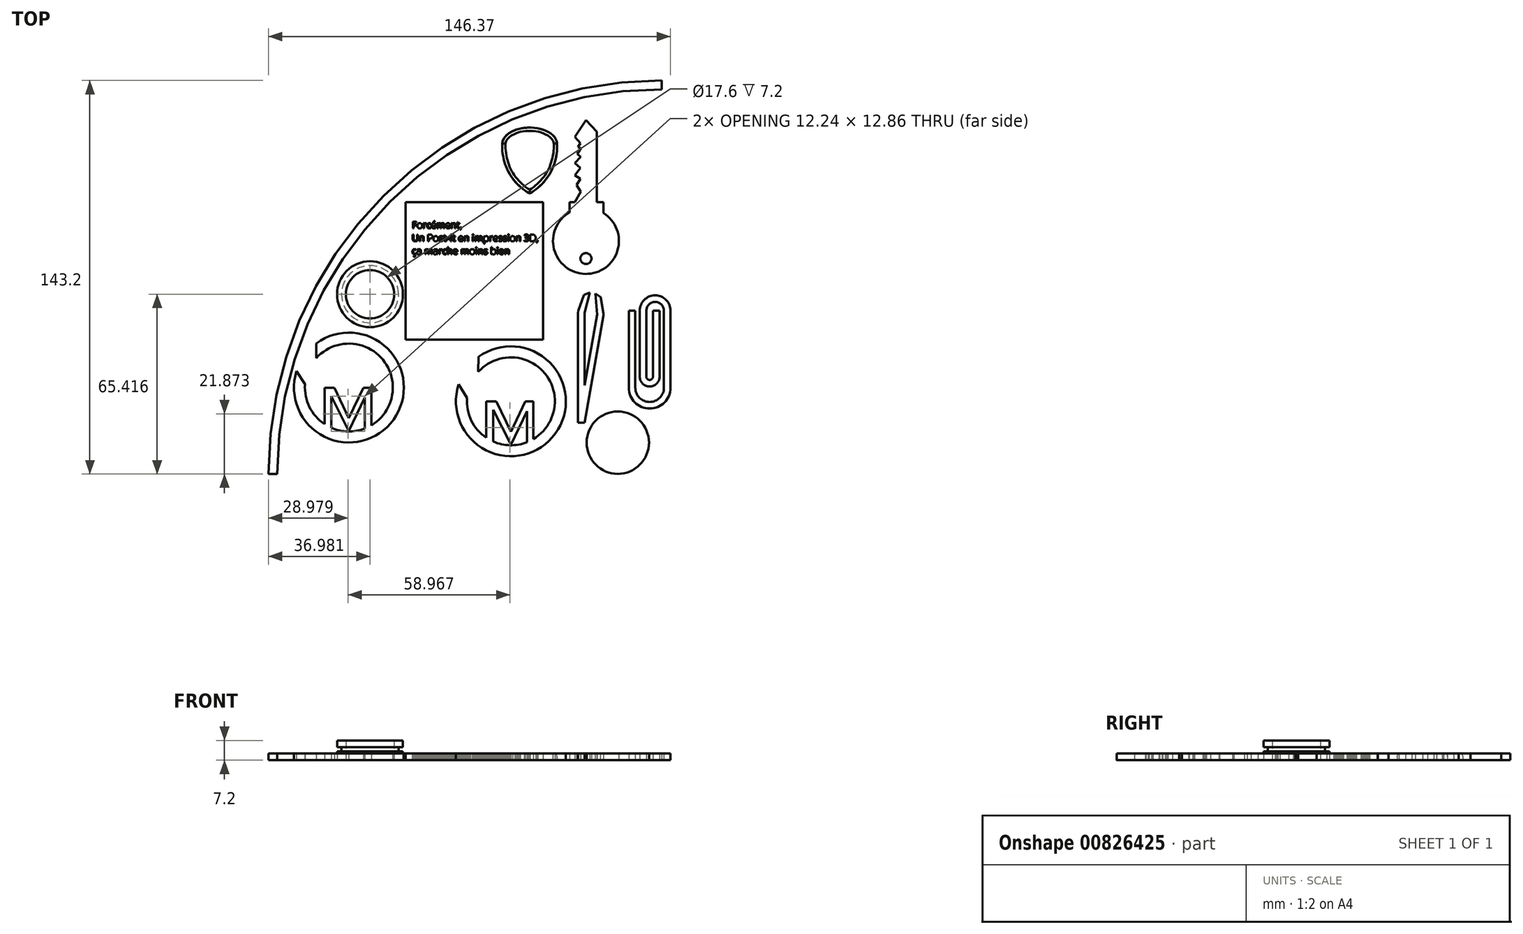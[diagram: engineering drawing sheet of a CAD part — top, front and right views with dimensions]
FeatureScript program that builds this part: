
annotation { "Feature Type Name" : "Feature", "Feature Type Description" : "" }
export const myFeature = defineFeature(function(context is Context, id is Id, definition is map)
    precondition{}
    {
        {
            var Q0;
            Q0=qCreatedBy(makeId("Top.planeOp"),FACE);
            var sketch = newSketch(context, id + "F0", { "sketchPlane" : qUnion([Q0])});
            skArc(sketch, "E0", {"start": v(69.34, 66.2) * mm, "mid": v(-29.65, 25.2) * mm, "end": v(-70.66, -73.8) * mm});
            skArc(sketch, "E1.0", {"start": v(69.34, 69.4) * mm, "mid": v(-31.91, 27.47) * mm, "end": v(-73.86, -73.8) * mm});
            skLineSegment(sketch, "E2", {"start": v(-70.66, -73.8) * mm, "end": v(-73.86, -73.8) * mm});
            skLineSegment(sketch, "E3", {"start": v(69.34, 66.2) * mm, "end": v(69.34, 69.4) * mm});
            skLineSegment(sketch, "E4.bottom", {"start": v(58.9, 56.22) * mm, "end": v(55.7, 56.22) * mm});
            skLineSegment(sketch, "E4.top", {"start": v(58.9, 24.22) * mm, "end": v(55.7, 24.22) * mm});
            skLineSegment(sketch, "E4.right", {"start": v(55.7, 56.22) * mm, "end": v(55.7, 24.22) * mm});
            skPoint(sketch, "E5.end.orphan", {"position": v(61.85, 21.02) * mm});
            skPoint(sketch, "E6.end.orphan", {"position": v(65.05, 21.02) * mm});
            skCircle(sketch, "E7", {"center": v(41.73, 11) * mm, "radius": 12 * mm});
            skCircle(sketch, "E8", {"center": v(41.73, 4.6) * mm, "radius": 2 * mm});
            skLineSegment(sketch, "E9", {"start": v(41.73, 11) * mm, "end": v(41.73, 55) * mm});
            skLineSegment(sketch, "E10", {"start": v(35.73, 25.17) * mm, "end": v(35.73, 21.4) * mm});
            skLineSegment(sketch, "E11", {"start": v(48.13, 25.17) * mm, "end": v(48.13, 21.15) * mm});
            skLineSegment(sketch, "E12", {"start": v(48.13, 25.17) * mm, "end": v(35.73, 25.17) * mm});
            skLineSegment(sketch, "E13", {"start": v(41.73, 25.17) * mm, "end": v(45.73, 25.17) * mm});
            skPoint(sketch, "E13.startSnap0", {"position": v(41.93, 25.17) * mm});
            skLineSegment(sketch, "E14", {"start": v(45.73, 25.17) * mm, "end": v(37.73, 25.17) * mm});
            skLineSegment(sketch, "E15.bottom", {"start": v(37.73, 25.17) * mm, "end": v(45.73, 25.17) * mm});
            skLineSegment(sketch, "E15.top", {"start": v(37.73, 25.17) * mm, "end": v(45.73, 25.17) * mm});
            skLineSegment(sketch, "E15.left", {"start": v(21.23, 18.77) * mm, "end": v(21.23, 18.77) * mm});
            skLineSegment(sketch, "E15.right", {"start": v(29.23, 18.77) * mm, "end": v(29.23, 18.77) * mm});
            skLineSegment(sketch, "E16", {"start": v(45.73, 25.17) * mm, "end": v(45.73, 50.72) * mm});
            skLineSegment(sketch, "E17", {"start": v(37.73, 40.09) * mm, "end": v(37.73, 39.31) * mm});
            skLineSegment(sketch, "E18", {"start": v(41.73, 55) * mm, "end": v(37.73, 48.82) * mm});
            skLineSegment(sketch, "E19", {"start": v(37.73, 48.82) * mm, "end": v(41.73, 55) * mm});
            skLineSegment(sketch, "E20", {"start": v(41.73, 55) * mm, "end": v(45.73, 50.72) * mm});
            skLineSegment(sketch, "E21", {"start": v(37.73, 48.82) * mm, "end": v(39.73, 46.63) * mm});
            skPoint(sketch, "E21.endSnap0", {"position": v(39.73, 51.91) * mm});
            skLineSegment(sketch, "E22", {"start": v(39.73, 46.63) * mm, "end": v(38.83, 45.25) * mm});
            skLineSegment(sketch, "E23", {"start": v(38.83, 45.25) * mm, "end": v(39.77, 44.64) * mm});
            skLineSegment(sketch, "E24", {"start": v(39.77, 44.64) * mm, "end": v(38.53, 42.71) * mm});
            skLineSegment(sketch, "E25", {"start": v(38.53, 42.71) * mm, "end": v(39.77, 41.6) * mm});
            skLineSegment(sketch, "E26", {"start": v(39.77, 41.6) * mm, "end": v(37.73, 39.31) * mm});
            skPoint(sketch, "E26.endSnap0", {"position": v(37.73, 40.09) * mm});
            skLineSegment(sketch, "E27", {"start": v(37.73, 39.31) * mm, "end": v(39.73, 37.53) * mm});
            skLineSegment(sketch, "E28", {"start": v(39.73, 37.53) * mm, "end": v(37.73, 34.88) * mm});
            skLineSegment(sketch, "E29", {"start": v(37.73, 34.88) * mm, "end": v(39.73, 33.59) * mm});
            skLineSegment(sketch, "E30", {"start": v(39.73, 33.59) * mm, "end": v(38.32, 31.4) * mm});
            skLineSegment(sketch, "E31", {"start": v(38.32, 31.4) * mm, "end": v(39.77, 28.88) * mm});
            skLineSegment(sketch, "E32", {"start": v(39.77, 28.88) * mm, "end": v(37.73, 25.17) * mm});
            skLineSegment(sketch, "E33", {"start": v(41.73, 25.17) * mm, "end": v(40.93, 25.17) * mm});
            skLineSegment(sketch, "E34", {"start": v(40.93, 25.17) * mm, "end": v(42.53, 25.17) * mm});
            skLineSegment(sketch, "E35", {"start": v(42.53, 25.17) * mm, "end": v(42.53, 54.15) * mm});
            skLineSegment(sketch, "E36", {"start": v(41.17, 54.15) * mm, "end": v(40.93, 25.17) * mm});
            skPoint(sketch, "E37.orphan", {"position": v(37.73, 55) * mm});
            skCircle(sketch, "E38", {"center": v(53.3, -62.4) * mm, "radius": 11.35 * mm});
            skCircle(sketch, "E39", {"center": v(-36.88, -8.37) * mm, "radius": 8.8 * mm});
            skCircle(sketch, "E40", {"center": v(-36.88, -8.37) * mm, "radius": 12 * mm});
            skEllipticalArc(sketch, "E41", {});
            skEllipticalArc(sketch, "E42", {});
            skPoint(sketch, "E43", {"position": v(11.23, 39.87) * mm});
            skPoint(sketch, "E44", {"position": v(12.95, 43.23) * mm});
            skPoint(sketch, "E45", {"position": v(29.5, 43.23) * mm});
            skPoint(sketch, "E46", {"position": v(31.23, 39.87) * mm});
            skEllipticalArc(sketch, "E47.trimOffspring", {});
            skLineSegment(sketch, "E48.bottom", {"start": v(26.09, 25.12) * mm, "end": v(-23.91, 25.12) * mm});
            skLineSegment(sketch, "E48.top", {"start": v(26.09, -24.88) * mm, "end": v(-23.91, -24.88) * mm});
            skLineSegment(sketch, "E48.left", {"start": v(26.09, 25.12) * mm, "end": v(26.09, -24.88) * mm});
            skLineSegment(sketch, "E48.right", {"start": v(-23.91, 25.12) * mm, "end": v(-23.91, -24.88) * mm});
            skText(sketch, "E49", { "text": "Forcément, \nUn Post-It en impression 3D,\nça marche moins bien", "fontName": "OpenSans-Regular.ttf"});
            skLineSegment(sketch, "E50.left", {"start": v(38.83, -15.16) * mm, "end": v(38.83, -55.16) * mm});
            skLineSegment(sketch, "E50.right", {"start": v(41.23, -15.16) * mm, "end": v(41.23, -41.55) * mm});
            skLineSegment(sketch, "E51.left", {"start": v(45.78, -15.77) * mm, "end": v(41.23, -41.55) * mm});
            skLineSegment(sketch, "E51.right", {"start": v(48.14, -16.18) * mm, "end": v(41.27, -55.16) * mm});
            skLineSegment(sketch, "E52", {"start": v(45.18, -7.75) * mm, "end": v(46.75, -7.47) * mm});
            skLineSegment(sketch, "E53", {"start": v(46.75, -7.47) * mm, "end": v(48.14, -15.35) * mm});
            skLineSegment(sketch, "E54", {"start": v(45.18, -7.75) * mm, "end": v(45.78, -15.77) * mm});
            skLineSegment(sketch, "E55", {"start": v(48.14, -15.35) * mm, "end": v(48.14, -16.18) * mm});
            skLineSegment(sketch, "E56", {"start": v(38.98, -14.34) * mm, "end": v(41.71, -6.82) * mm});
            skLineSegment(sketch, "E57", {"start": v(41.71, -6.82) * mm, "end": v(43.22, -7.37) * mm});
            skLineSegment(sketch, "E58", {"start": v(43.22, -7.37) * mm, "end": v(41.23, -15.16) * mm});
            skLineSegment(sketch, "E59", {"start": v(38.98, -14.34) * mm, "end": v(38.83, -15.16) * mm});
            skLineSegment(sketch, "E60", {"start": v(38.83, -55.16) * mm, "end": v(41.27, -55.16) * mm});
            skLineSegment(sketch, "E61.bottom", {"start": v(61.3, -14.39) * mm, "end": v(63.7, -14.39) * mm});
            skLineSegment(sketch, "E61.left", {"start": v(61.3, -14.39) * mm, "end": v(61.3, -38.39) * mm});
            skLineSegment(sketch, "E61.right", {"start": v(63.7, -14.39) * mm, "end": v(63.7, -38.39) * mm});
            skLineSegment(sketch, "E62.bottom", {"start": v(70.1, -14.39) * mm, "end": v(72.5, -14.39) * mm});
            skLineSegment(sketch, "E62.top", {"start": v(70.1, -42.39) * mm, "end": v(72.5, -42.39) * mm});
            skLineSegment(sketch, "E62.left", {"start": v(70.1, -14.39) * mm, "end": v(70.1, -42.39) * mm});
            skLineSegment(sketch, "E62.right", {"start": v(72.5, -14.39) * mm, "end": v(72.5, -42.39) * mm});
            skArc(sketch, "E63", {"start": v(70.1, -14.39) * mm, "mid": v(66.9, -11.19) * mm, "end": v(63.7, -14.39) * mm});
            skArc(sketch, "E64.0", {"start": v(72.5, -14.39) * mm, "mid": v(66.9, -8.79) * mm, "end": v(61.3, -14.39) * mm});
            skLineSegment(sketch, "E65.bottom", {"start": v(57.3, -14.39) * mm, "end": v(59.7, -14.39) * mm});
            skLineSegment(sketch, "E65.top", {"start": v(57.3, -42.39) * mm, "end": v(59.7, -42.39) * mm});
            skLineSegment(sketch, "E65.left", {"start": v(57.3, -14.39) * mm, "end": v(57.3, -42.39) * mm});
            skLineSegment(sketch, "E65.right", {"start": v(59.7, -14.39) * mm, "end": v(59.7, -42.39) * mm});
            skArc(sketch, "E66", {"start": v(59.7, -42.39) * mm, "mid": v(64.9, -47.59) * mm, "end": v(70.1, -42.39) * mm});
            skArc(sketch, "E67.0", {"start": v(57.3, -42.39) * mm, "mid": v(64.9, -49.99) * mm, "end": v(72.5, -42.39) * mm});
            skArc(sketch, "E68", {"start": v(-1.55, -46.1) * mm, "mid": v(0, -54.32) * mm, "end": v(5.47, -60.63) * mm});
            skArc(sketch, "E69.0", {"start": v(-4.64, -41.22) * mm, "mid": v(30.59, -59.1) * mm, "end": v(2.65, -31.17) * mm});
            skLineSegment(sketch, "E70", {"start": v(-4.64, -41.22) * mm, "end": v(-1.55, -46.1) * mm});
            skLineSegment(sketch, "E71", {"start": v(2.65, -31.17) * mm, "end": v(2.54, -36.61) * mm});
            skPoint(sketch, "E72.end.orphan", {"position": v(27.87, -32.5) * mm});
            skLineSegment(sketch, "E73", {"start": v(61.3, -38.39) * mm, "end": v(63.7, -38.39) * mm});
            skPoint(sketch, "E61.top.start.orphan", {"position": v(61.3, -42.39) * mm});
            skLineSegment(sketch, "E74.bottom", {"start": v(66.1, -14.39) * mm, "end": v(68.5, -14.39) * mm});
            skLineSegment(sketch, "E74.left", {"start": v(66.1, -14.39) * mm, "end": v(66.1, -38.39) * mm});
            skLineSegment(sketch, "E74.right", {"start": v(68.5, -14.39) * mm, "end": v(68.5, -38.39) * mm});
            skLineSegment(sketch, "E75", {"start": v(66.1, -38.39) * mm, "end": v(68.5, -38.39) * mm});
            skArc(sketch, "E76", {"start": v(63.7, -38.39) * mm, "mid": v(64.9, -39.59) * mm, "end": v(66.1, -38.39) * mm});
            skArc(sketch, "E77.0", {"start": v(61.3, -38.39) * mm, "mid": v(64.9, -41.99) * mm, "end": v(68.5, -38.39) * mm});
            skLineSegment(sketch, "E78", {"start": v(5.47, -60.63) * mm, "end": v(5.47, -47.4) * mm});
            skLineSegment(sketch, "E79", {"start": v(5.47, -47.4) * mm, "end": v(9.08, -47.4) * mm});
            skLineSegment(sketch, "E80", {"start": v(9.08, -47.4) * mm, "end": v(14.4, -58.43) * mm});
            skLineSegment(sketch, "E81", {"start": v(14.4, -58.43) * mm, "end": v(19.67, -47.4) * mm});
            skLineSegment(sketch, "E82", {"start": v(19.67, -47.4) * mm, "end": v(22.6, -47.4) * mm});
            skLineSegment(sketch, "E83", {"start": v(22.6, -47.4) * mm, "end": v(22.6, -61.09) * mm});
            skLineSegment(sketch, "E84", {"start": v(20.2, -61.09) * mm, "end": v(20.2, -62.26) * mm});
            skLineSegment(sketch, "E85", {"start": v(20.2, -62.26) * mm, "end": v(20.2, -51) * mm});
            skLineSegment(sketch, "E86", {"start": v(20.2, -51) * mm, "end": v(14.4, -63.16) * mm});
            skLineSegment(sketch, "E87", {"start": v(7.96, -62) * mm, "end": v(7.96, -50.49) * mm});
            skLineSegment(sketch, "E88", {"start": v(7.96, -50.49) * mm, "end": v(14.4, -63.16) * mm});
            skPoint(sketch, "E89.orphan", {"position": v(7.42, -51) * mm});
            skPoint(sketch, "E90.orphan", {"position": v(20.2, -47.4) * mm});
            skArc(sketch, "E91.trimOffspring", {"start": v(22.6, -61.09) * mm, "mid": v(26.77, -37.21) * mm, "end": v(2.54, -36.61) * mm});
            skArc(sketch, "E92.trimOffspring", {"start": v(7.96, -62) * mm, "mid": v(14.06, -63.35) * mm, "end": v(20.2, -62.26) * mm});
            skArc(sketch, "E93", {"start": v(-60.53, -41.21) * mm, "mid": v(-58.92, -49.42) * mm, "end": v(-53.4, -55.7) * mm});
            skArc(sketch, "E94.0", {"start": v(-63.65, -36.35) * mm, "mid": v(-28.3, -53.98) * mm, "end": v(-56.43, -26.25) * mm});
            skLineSegment(sketch, "E95", {"start": v(-63.65, -36.35) * mm, "end": v(-60.53, -41.21) * mm});
            skLineSegment(sketch, "E96", {"start": v(-56.43, -26.25) * mm, "end": v(-56.43, -31.61) * mm});
            skPoint(sketch, "E97.end.orphan", {"position": v(-30.95, -27.71) * mm});
            skLineSegment(sketch, "E98", {"start": v(-53.4, -55.7) * mm, "end": v(-53.4, -42.4) * mm});
            skLineSegment(sketch, "E99", {"start": v(-53.4, -42.4) * mm, "end": v(-49.88, -42.4) * mm});
            skLineSegment(sketch, "E100", {"start": v(-49.88, -42.4) * mm, "end": v(-44.57, -53.43) * mm});
            skLineSegment(sketch, "E101", {"start": v(-44.57, -53.43) * mm, "end": v(-39.3, -42.4) * mm});
            skLineSegment(sketch, "E102", {"start": v(-39.3, -42.4) * mm, "end": v(-36.36, -42.4) * mm});
            skLineSegment(sketch, "E103", {"start": v(-36.36, -42.4) * mm, "end": v(-36.36, -56.09) * mm});
            skLineSegment(sketch, "E104", {"start": v(-38.76, -56.09) * mm, "end": v(-38.76, -57.26) * mm});
            skLineSegment(sketch, "E105", {"start": v(-38.76, -57.26) * mm, "end": v(-38.76, -46) * mm});
            skLineSegment(sketch, "E106", {"start": v(-38.76, -46) * mm, "end": v(-44.57, -58.16) * mm});
            skLineSegment(sketch, "E107", {"start": v(-51, -57) * mm, "end": v(-51, -45.48) * mm});
            skLineSegment(sketch, "E108", {"start": v(-51, -45.48) * mm, "end": v(-44.57, -58.16) * mm});
            skPoint(sketch, "E109.orphan", {"position": v(-51.55, -46) * mm});
            skPoint(sketch, "E110.orphan", {"position": v(-38.76, -42.4) * mm});
            skArc(sketch, "E111.trimOffspring", {"start": v(-36.36, -56.09) * mm, "mid": v(-32.2, -32.2) * mm, "end": v(-56.43, -31.61) * mm});
            skArc(sketch, "E112.trimOffspring", {"start": v(-51, -57) * mm, "mid": v(-44.9, -58.35) * mm, "end": v(-38.76, -57.26) * mm});
            skLineSegment(sketch, "E113.top", {"start": v(-19.06, -66.6) * mm, "end": v(-14.26, -66.6) * mm});
            skLineSegment(sketch, "E113.right", {"start": v(-14.26, -28.28) * mm, "end": v(-14.26, -66.6) * mm});
            skLineSegment(sketch, "E114", {"start": v(-14.26, -66.6) * mm, "end": v(1.74, -66.6) * mm});
            skLineSegment(sketch, "E115", {"start": v(1.74, -66.6) * mm, "end": v(1.74, -70.2) * mm});
            skLineSegment(sketch, "E116", {"start": v(-14.26, -73.8) * mm, "end": v(-19.06, -73.8) * mm});
            skLineSegment(sketch, "E117", {"start": v(-35.06, -70.2) * mm, "end": v(-35.06, -66.6) * mm});
            skLineSegment(sketch, "E118", {"start": v(-35.06, -66.6) * mm, "end": v(-19.06, -66.6) * mm});
            skLineSegment(sketch, "E119", {"start": v(-16.66, -28.28) * mm, "end": v(-14.26, -28.28) * mm});
            skLineSegment(sketch, "E120", {"start": v(-14.26, -66.6) * mm, "end": v(-16.66, -66.6) * mm});
            skPoint(sketch, "E121.orphan", {"position": v(-19.06, -28.28) * mm});
            skLineSegment(sketch, "E122", {"start": v(-19.06, -66.6) * mm, "end": v(-19.06, -73.8) * mm});
            skLineSegment(sketch, "E123", {"start": v(-14.26, -66.6) * mm, "end": v(-14.26, -73.8) * mm});
            skPoint(sketch, "E124.orphan", {"position": v(-35.06, -73.8) * mm});
            skPoint(sketch, "E125.end.orphan", {"position": v(1.74, -73.8) * mm});
            skLineSegment(sketch, "E126", {"start": v(58.9, 11.82) * mm, "end": v(55.7, 24.22) * mm});
            skLineSegment(sketch, "E127", {"start": v(55.7, 56.22) * mm, "end": v(62.1, 56.22) * mm});
            skLineSegment(sketch, "E128", {"start": v(62.1, 56.22) * mm, "end": v(62.1, 23.65) * mm});
            skLineSegment(sketch, "E129", {"start": v(55.7, 24.22) * mm, "end": v(62.1, 24.22) * mm});
            skLineSegment(sketch, "E130", {"start": v(62.1, 24.22) * mm, "end": v(58.9, 11.82) * mm});
            skLineSegment(sketch, "E131", {"start": v(-16.66, -28.28) * mm, "end": v(-19.06, -28.28) * mm});
            skLineSegment(sketch, "E132", {"start": v(-19.06, -66.6) * mm, "end": v(-19.06, -28.28) * mm});
            skLineSegment(sketch, "E133", {"start": v(-35.06, -70.2) * mm, "end": v(-35.06, -73.8) * mm});
            skLineSegment(sketch, "E134", {"start": v(1.74, -70.2) * mm, "end": v(1.74, -73.8) * mm});
            skLineSegment(sketch, "E135", {"start": v(-35.06, -73.8) * mm, "end": v(1.74, -73.8) * mm});
            skPoint(sketch, "E136.end.orphan", {"position": v(-19.06, -70.2) * mm});
            skPoint(sketch, "E137.start.orphan", {"position": v(-14.26, -70.2) * mm});
            const initialGuessF0  = {"E41": [0.021226862445473664, 0.04626882898807526, 1, 0, 0.01, 0.006, 0, 3.141592653589793], "E42": [0.011226862445473662, 0.04626882898807526, 0.48564293117863244, -0.8741572761215376, 0.02059126028197401, 0.01982755325631149, 0, 1.0929807321065532], "E47.trimOffspring": [0.031226862445473666, 0.04626882898807526, -0.4856429311786319, -0.8741572761215379, 0.020591260281974, 0.01982755325631149, 5.190204575073031, 0], "E49": [-0.02165, 0.0156, 1, 0, 0.0025]};
            skSetInitialGuess(sketch, initialGuessF0);
            skSolve(sketch);
        }
        {
            var Q0;
            {var subQ1=sQuery(id+"F0.wireOp",EDGE,"E41");var subQ4=sQuery(id+"F0.wireOp",EDGE,"E42");var subQ6=makeQuery(id+"F0.imprint","INTERSECT",VERTEX,{"disambiguationData":[OD(1.0)],"derivedFrom":[subQ1,subQ4]});Q0=makeQuery(id+"F0.imprint","IMPRINT",FACE,{"disambiguationData":[TD([[makeQuery(id+"F0.imprint","IMPRINT",EDGE,{"disambiguationData":[TD([[subQ6,-1.0]])],"derivedFrom":subQ1}),1.0]])]});}
            var Q1;
            Q1=makeQuery(id+"F0.imprint","IMPRINT",FACE,{"disambiguationData":[TD([[makeQuery(id+"F0.imprint","IMPRINT",EDGE,{"derivedFrom":sQuery(id+"F0.wireOp",EDGE,"E0")}),-1.0]])]});
            var Q2;
            Q2=makeQuery(id+"F0.imprint","IMPRINT",FACE,{"disambiguationData":[TD([[makeQuery(id+"F0.imprint","IMPRINT",EDGE,{"derivedFrom":sQuery(id+"F0.wireOp",EDGE,"E50.left")}),1.0]])]});
            var Q3;
            Q3=makeQuery(id+"F0.imprint","IMPRINT",FACE,{"disambiguationData":[TD([[makeQuery(id+"F0.imprint","IMPRINT",EDGE,{"derivedFrom":sQuery(id+"F0.wireOp",EDGE,"E65.bottom")}),-1.0]])]});
            var Q4;
            Q4=makeQuery(id+"F0.imprint","IMPRINT",FACE,{"disambiguationData":[TD([[makeQuery(id+"F0.imprint","IMPRINT",EDGE,{"derivedFrom":sQuery(id+"F0.wireOp",EDGE,"E62.top")}),-1.0]])]});
            var Q5;
            Q5=makeQuery(id+"F0.imprint","IMPRINT",FACE,{"disambiguationData":[TD([[makeQuery(id+"F0.imprint","IMPRINT",EDGE,{"derivedFrom":sQuery(id+"F0.wireOp",EDGE,"E62.bottom")}),-1.0]])]});
            var Q6;
            Q6=makeQuery(id+"F0.imprint","IMPRINT",FACE,{"disambiguationData":[TD([[makeQuery(id+"F0.imprint","IMPRINT",EDGE,{"derivedFrom":sQuery(id+"F0.wireOp",EDGE,"E61.bottom")}),1.0]])]});
            var Q7;
            Q7=makeQuery(id+"F0.imprint","IMPRINT",FACE,{"disambiguationData":[TD([[makeQuery(id+"F0.imprint","IMPRINT",EDGE,{"derivedFrom":sQuery(id+"F0.wireOp",EDGE,"E61.bottom")}),-1.0]])]});
            var Q8;
            Q8=makeQuery(id+"F0.imprint","IMPRINT",FACE,{"disambiguationData":[TD([[makeQuery(id+"F0.imprint","IMPRINT",EDGE,{"derivedFrom":sQuery(id+"F0.wireOp",EDGE,"E38")}),1.0]])]});
            var Q9;
            Q9=makeQuery(id+"F0.imprint","IMPRINT",FACE,{"disambiguationData":[TD([[makeQuery(id+"F0.imprint","IMPRINT",EDGE,{"derivedFrom":sQuery(id+"F0.wireOp",EDGE,"E48.bottom")}),1.0]])]});
            var Q10;
            Q10=makeQuery(id+"F0.imprint","IMPRINT",FACE,{"disambiguationData":[TD([[makeQuery(id+"F0.imprint","IMPRINT",EDGE,{"derivedFrom":sQuery(id+"F0.wireOp",EDGE,"E73")}),-1.0]])]});
            var Q11;
            Q11=makeQuery(id+"F0.imprint","IMPRINT",FACE,{"disambiguationData":[TD([[makeQuery(id+"F0.imprint","IMPRINT",EDGE,{"derivedFrom":sQuery(id+"F0.wireOp",EDGE,"E74.bottom")}),-1.0]])]});
            var Q12;
            Q12=makeQuery(id+"F0.imprint","IMPRINT",FACE,{"disambiguationData":[TD([[makeQuery(id+"F0.imprint","IMPRINT",EDGE,{"derivedFrom":sQuery(id+"F0.wireOp",EDGE,"E93")}),-1.0]])]});
            var Q13;
            Q13=makeQuery(id+"F0.imprint","IMPRINT",FACE,{"disambiguationData":[TD([[makeQuery(id+"F0.imprint","IMPRINT",EDGE,{"derivedFrom":sQuery(id+"F0.wireOp",EDGE,"E68")}),-1.0]])]});
            extrude(context, id + "F1", {"entities" : qUnion([Q0, Q1, Q2, Q3, Q4, Q5, Q6, Q7, Q8, Q9, Q10, Q11, Q12, Q13]), "depth" : 2.4 * mm, "offsetDistance" : 25 * mm});
        }
        {
            var Q0;
            Q0=makeQuery(id+"F1.opExtrude","CAP_EDGE",EDGE,{"disambiguationData":[OSD([sQuery(id+"F0.wireOp",EDGE,"E42")])],"isStart":false});
            var Q1;
            Q1=makeQuery(id+"F1.opExtrude","CAP_EDGE",EDGE,{"disambiguationData":[OSD([sQuery(id+"F0.wireOp",EDGE,"E47.trimOffspring")])],"isStart":false});
            var Q2;
            Q2=makeQuery(id+"F1.opExtrude","CAP_EDGE",EDGE,{"disambiguationData":[OSD([sQuery(id+"F0.wireOp",EDGE,"E41")])],"isStart":false});
            fillet(context, id + "F2", {"entities" : qUnion([Q0, Q1, Q2]), "radius" : 1.2 * mm, "tangentPropagation" : true, "allowEdgeOverflow" : false});
        }
        {
            var Q0;
            {var subQ3=sQuery(id+"F0.wireOp",EDGE,"E21");Q0=makeQuery(id+"F0.imprint","IMPRINT",FACE,{"disambiguationData":[TD([[makeQuery(id+"F0.imprint","IMPRINT",EDGE,{"derivedFrom":subQ3}),1.0]])]});}
            var Q1;
            {var subQ0=sQuery(id+"F0.wireOp",EDGE,"E16");Q1=makeQuery(id+"F0.imprint","IMPRINT",FACE,{"disambiguationData":[TD([[makeQuery(id+"F0.imprint","IMPRINT",EDGE,{"derivedFrom":subQ0}),1.0]])]});}
            var Q2;
            {var subQ1=sQuery(id+"F0.wireOp",EDGE,"E10");Q2=makeQuery(id+"F0.imprint","IMPRINT",FACE,{"disambiguationData":[TD([[makeQuery(id+"F0.imprint","IMPRINT",EDGE,{"derivedFrom":subQ1}),1.0]])]});}
            var Q3;
            {var subQ1=sQuery(id+"F0.wireOp",EDGE,"E11");Q3=makeQuery(id+"F0.imprint","IMPRINT",FACE,{"disambiguationData":[TD([[makeQuery(id+"F0.imprint","IMPRINT",EDGE,{"derivedFrom":subQ1}),-1.0]])]});}
            var Q4;
            Q4=makeQuery(id+"F0.imprint","IMPRINT",FACE,{"disambiguationData":[TD([[makeQuery(id+"F0.imprint","IMPRINT",EDGE,{"derivedFrom":sQuery(id+"F0.wireOp",EDGE,"E8")}),-1.0]])]});
            var Q5;
            {var subQ5=sQuery(id+"F0.wireOp",EDGE,"E35");Q5=makeQuery(id+"F0.imprint","IMPRINT",FACE,{"disambiguationData":[TD([[makeQuery(id+"F0.imprint","IMPRINT",EDGE,{"derivedFrom":subQ5}),1.0]])]});}
            var Q6;
            {var subQ5=sQuery(id+"F0.wireOp",EDGE,"E36");Q6=makeQuery(id+"F0.imprint","IMPRINT",FACE,{"disambiguationData":[TD([[makeQuery(id+"F0.imprint","IMPRINT",EDGE,{"derivedFrom":subQ5}),1.0]])]});}
            extrude(context, id + "F3", {"entities" : qUnion([Q0, Q1, Q2, Q3, Q4, Q5, Q6]), "depth" : 2.4 * mm, "offsetDistance" : 25 * mm});
        }
        {
            var Q0;
            Q0=makeQuery(id+"F0.imprint","IMPRINT",FACE,{"disambiguationData":[TD([[makeQuery(id+"F0.imprint","IMPRINT",EDGE,{"derivedFrom":sQuery(id+"F0.wireOp",EDGE,"E39")}),-1.0]])]});
            extrude(context, id + "F4", {"entities" : qUnion([Q0]), "depth" : 3.2 * mm, "offsetDistance" : 25 * mm});
        }
        {
            var Q0;
            Q0=makeQuery(id+"F4.opExtrude","CAP_FACE",FACE,{"disambiguationData":[OSD([sQuery(id+"F0.wireOp",EDGE,"E39"),sQuery(id+"F0.wireOp",EDGE,"E40")])],"isStart":false});
            var sketch = newSketch(context, id + "F5", { "sketchPlane" : qUnion([Q0])});
            skCircle(sketch, "E138.0", {"center": v(-36.88, -8.37) * mm, "radius": 10.4 * mm});
            skSolve(sketch);
        }
        {
            var Q0;
            Q0=makeQuery(id+"F5.imprint","IMPRINT",FACE,{"disambiguationData":[TD([[makeQuery(id+"F5.imprint","IMPRINT",EDGE,{"derivedFrom":sQuery(id+"F5.wireOp",EDGE,"E138.0")}),1.0]])]});
            extrude(context, id + "F6", {"entities" : qUnion([Q0]), "operationType" : NewBodyOperationType.ADD, "depth" : 1.6 * mm, "offsetDistance" : 25 * mm});
        }
        {
            var Q0;
            Q0=makeQuery(id+"F6.opExtrude","CAP_FACE",FACE,{"disambiguationData":[OSD([sQuery(id+"F0.wireOp",EDGE,"E39"),sQuery(id+"F5.wireOp",EDGE,"E138.0")])],"isStart":false});
            var sketch = newSketch(context, id + "F7", { "sketchPlane" : qUnion([Q0])});
            skCircle(sketch, "E139.0", {"center": v(-36.88, -8.37) * mm, "radius": 12 * mm});
            skSolve(sketch);
        }
        {
            var Q0;
            Q0=makeQuery(id+"F7.imprint","IMPRINT",FACE,{"disambiguationData":[TD([[makeQuery(id+"F7.imprint","IMPRINT",EDGE,{"derivedFrom":makeQuery(id+"F6.opExtrude","CAP_EDGE",EDGE,{"disambiguationData":[OSD([sQuery(id+"F5.wireOp",EDGE,"E138.0")])],"isStart":false})}),1.0]])]});
            var Q1;
            Q1=makeQuery(id+"F7.imprint","IMPRINT",FACE,{"disambiguationData":[TD([[makeQuery(id+"F7.imprint","IMPRINT",EDGE,{"derivedFrom":sQuery(id+"F7.wireOp",EDGE,"E139.0")}),1.0]])]});
            extrude(context, id + "F8", {"entities" : qUnion([Q0, Q1]), "operationType" : NewBodyOperationType.ADD, "depth" : 2.4 * mm, "offsetDistance" : 25 * mm});
        }
        {
            var Q0;
            Q0=makeQuery(id+"F1.opExtrude","SWEPT_EDGE",EDGE,{"disambiguationData":[OSD([sQuery(id+"F0.wireOp",EDGE,"E52"),sQuery(id+"F0.wireOp",EDGE,"E53")])]});
            var Q1;
            Q1=makeQuery(id+"F1.opExtrude","SWEPT_EDGE",EDGE,{"disambiguationData":[OSD([sQuery(id+"F0.wireOp",EDGE,"E56"),sQuery(id+"F0.wireOp",EDGE,"E57")])]});
            chamfer(context, id + "F9", {"entities" : qUnion([Q0, Q1]), "width" : 2 * mm, "tangentPropagation" : true});
        }
    });
